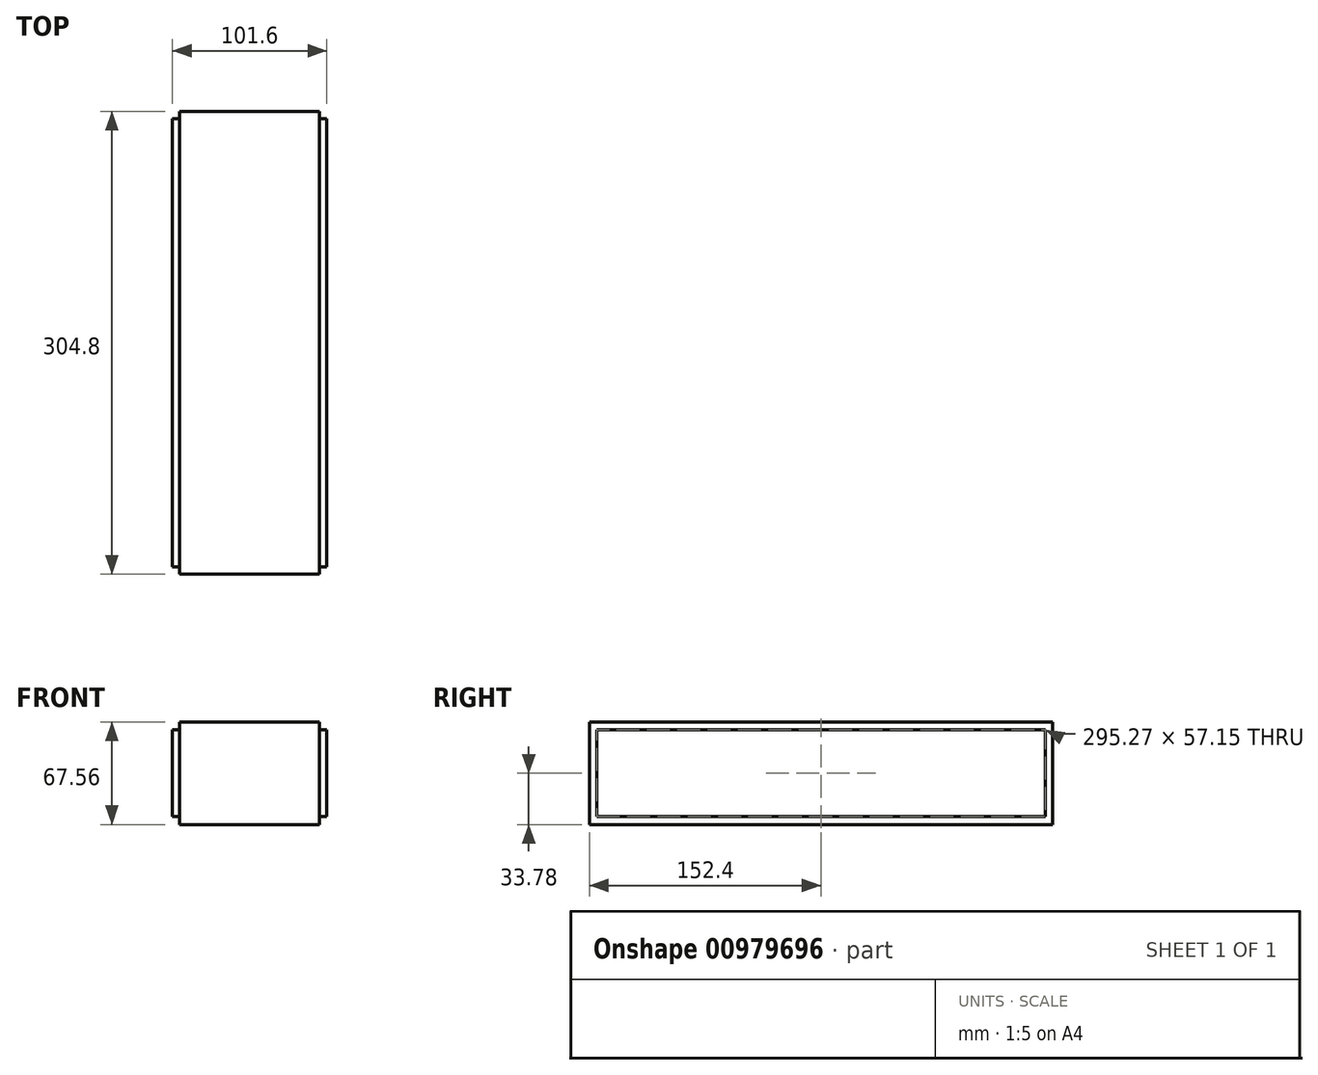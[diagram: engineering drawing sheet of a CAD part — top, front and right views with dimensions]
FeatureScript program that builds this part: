
annotation { "Feature Type Name" : "Feature", "Feature Type Description" : "" }
export const myFeature = defineFeature(function(context is Context, id is Id, definition is map)
    precondition{}
    {
        {
            var Q0;
            Q0=qCreatedBy(makeId("Right.planeOp"),FACE);
            var sketch = newSketch(context, id + "F0", { "sketchPlane" : qUnion([Q0])});
            skLineSegment(sketch, "E0.bottom", {"start": v(152.4, 33.78) * mm, "end": v(-152.4, 33.78) * mm});
            skLineSegment(sketch, "E0.top", {"start": v(152.4, -33.78) * mm, "end": v(-152.4, -33.78) * mm});
            skLineSegment(sketch, "E0.left", {"start": v(152.4, 33.78) * mm, "end": v(152.4, -33.78) * mm});
            skLineSegment(sketch, "E0.right", {"start": v(-152.4, 33.78) * mm, "end": v(-152.4, -33.78) * mm});
            skPoint(sketch, "E0.middle", {"position": v(0, 0) * mm});
            skLineSegment(sketch, "E1.bottom", {"start": v(147.64, -28.57) * mm, "end": v(-147.64, -28.58) * mm});
            skLineSegment(sketch, "E1.top", {"start": v(147.64, 28.58) * mm, "end": v(-147.64, 28.57) * mm});
            skLineSegment(sketch, "E1.left", {"start": v(147.64, -28.57) * mm, "end": v(147.64, 28.58) * mm});
            skLineSegment(sketch, "E1.right", {"start": v(-147.64, -28.58) * mm, "end": v(-147.64, 28.57) * mm});
            skSolve(sketch);
        }
        {
            var Q0;
            Q0=makeQuery(id+"F0.imprint","IMPRINT",FACE,{"disambiguationData":[TD([[makeQuery(id+"F0.imprint","IMPRINT",EDGE,{"derivedFrom":sQuery(id+"F0.wireOp",EDGE,"E0.bottom")}),1.0]])]});
            extrude(context, id + "F1", {"entities" : qUnion([Q0]), "endBound" : BoundingType.SYMMETRIC, "depth" : 92.07 * mm, "offsetDistance" : 25.4 * mm});
        }
        {
            var Q0;
            Q0=makeQuery(id+"F0.imprint","IMPRINT",FACE,{"disambiguationData":[TD([[makeQuery(id+"F0.imprint","IMPRINT",EDGE,{"derivedFrom":sQuery(id+"F0.wireOp",EDGE,"E1.bottom")}),-1.0]])]});
            extrude(context, id + "F2", {"entities" : qUnion([Q0]), "operationType" : NewBodyOperationType.ADD, "endBound" : BoundingType.SYMMETRIC, "depth" : 101.6 * mm, "offsetDistance" : 25.4 * mm});
        }
    });
